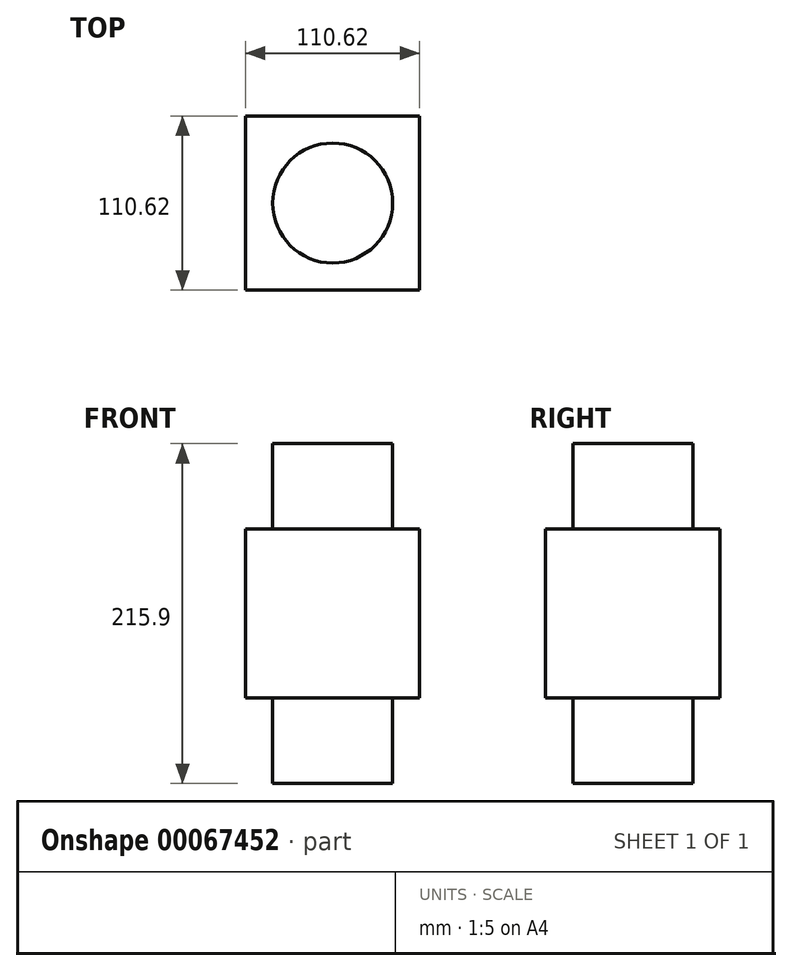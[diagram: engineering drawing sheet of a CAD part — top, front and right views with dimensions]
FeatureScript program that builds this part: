
annotation { "Feature Type Name" : "Feature", "Feature Type Description" : "" }
export const myFeature = defineFeature(function(context is Context, id is Id, definition is map)
    precondition{}
    {
        {
            var Q0;
            Q0=qCreatedBy(makeId("Top.planeOp"),FACE);
            var sketch = newSketch(context, id + "F0", { "sketchPlane" : qUnion([Q0])});
            skLineSegment(sketch, "E0.bottom", {"start": v(0, 0) * mm, "end": v(110.62, 0) * mm});
            skLineSegment(sketch, "E0.top", {"start": v(0, -110.62) * mm, "end": v(110.62, -110.62) * mm});
            skLineSegment(sketch, "E0.left", {"start": v(0, 0) * mm, "end": v(0, -110.62) * mm});
            skLineSegment(sketch, "E0.right", {"start": v(110.62, 0) * mm, "end": v(110.62, -110.62) * mm});
            skSolve(sketch);
        }
        {
            var Q0;
            Q0 = qSketchRegion(id + "F0", true);
            extrude(context, id + "F1", {"entities" : qUnion([Q0]), "depth" : 53.72 * mm, "hasSecondDirection" : true, "secondDirectionOppositeDirection" : true, "secondDirectionDepth" : 53.72 * mm});
        }
        {
            var Q0;
            Q0=makeQuery(id+"F1.opExtrude","CAP_FACE",FACE,{"disambiguationData":[OSD([sQuery(id+"F0.wireOp",EDGE,"E0.bottom"),sQuery(id+"F0.wireOp",EDGE,"E0.top"),sQuery(id+"F0.wireOp",EDGE,"E0.left"),sQuery(id+"F0.wireOp",EDGE,"E0.right")])],"isStart":false});
            var sketch = newSketch(context, id + "F2", { "sketchPlane" : qUnion([Q0])});
            skLineSegment(sketch, "E1", {"start": v(0, -110.62) * mm, "end": v(110.62, 0) * mm, "construction": true});
            skCircle(sketch, "E2", {"center": v(55.3, -55.3) * mm, "radius": 38.1 * mm});
            skSolve(sketch);
        }
        {
            var Q0;
            Q0 = qSketchRegion(id + "F2", true);
            extrude(context, id + "F3", {"entities" : qUnion([Q0]), "operationType" : NewBodyOperationType.ADD, "depth" : 54.23 * mm});
        }
        {
            var Q0;
            Q0=makeQuery(id+"F1.opExtrude","CAP_FACE",FACE,{"disambiguationData":[OSD([sQuery(id+"F0.wireOp",EDGE,"E0.bottom"),sQuery(id+"F0.wireOp",EDGE,"E0.top"),sQuery(id+"F0.wireOp",EDGE,"E0.left"),sQuery(id+"F0.wireOp",EDGE,"E0.right")])],"isStart":true});
            var sketch = newSketch(context, id + "F4", { "sketchPlane" : qUnion([Q0])});
            skLineSegment(sketch, "E3", {"start": v(0, 0) * mm, "end": v(110.62, 110.62) * mm, "construction": true});
            skCircle(sketch, "E4", {"center": v(55.3, 55.3) * mm, "radius": 38.1 * mm});
            skSolve(sketch);
        }
        {
            var Q0;
            Q0 = qSketchRegion(id + "F4", true);
            extrude(context, id + "F5", {"entities" : qUnion([Q0]), "operationType" : NewBodyOperationType.ADD, "depth" : 54.23 * mm});
        }
    });
